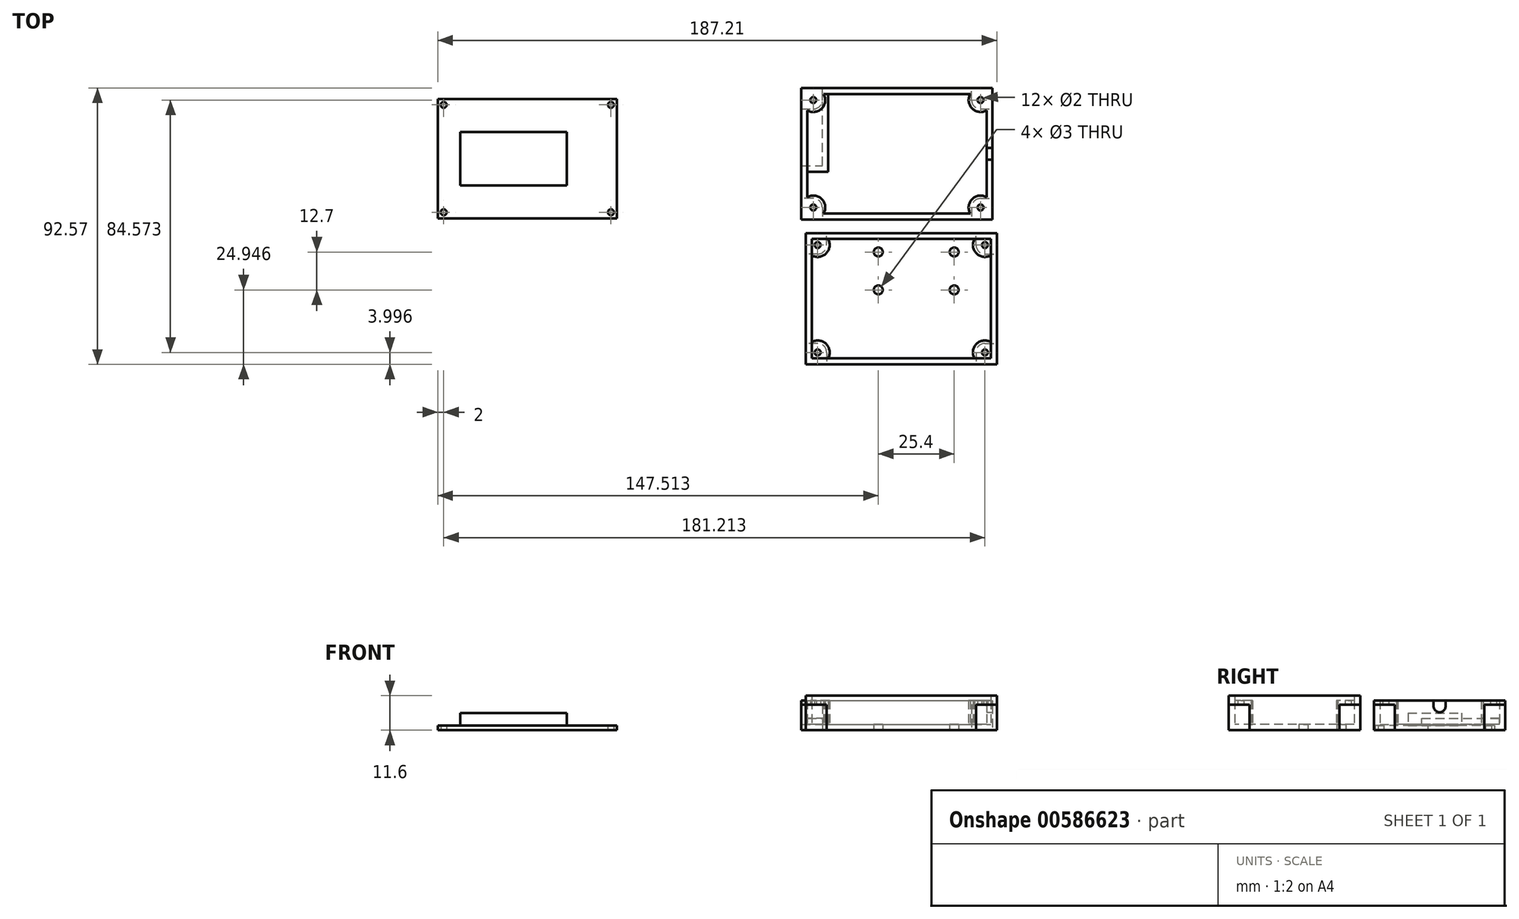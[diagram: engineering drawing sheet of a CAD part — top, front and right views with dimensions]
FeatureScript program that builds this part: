
annotation { "Feature Type Name" : "Feature", "Feature Type Description" : "" }
export const myFeature = defineFeature(function(context is Context, id is Id, definition is map)
    precondition{}
    {
        {
            var Q0;
            Q0=qCreatedBy(makeId("Top.planeOp"),FACE);
            var sketch = newSketch(context, id + "F0", { "sketchPlane" : qUnion([Q0])});
            skLineSegment(sketch, "E0.bottom", {"start": v(-101.7, 31.82) * mm, "end": v(-41.7, 31.82) * mm});
            skLineSegment(sketch, "E0.top", {"start": v(-101.7, -8.18) * mm, "end": v(-41.7, -8.18) * mm});
            skLineSegment(sketch, "E0.left", {"start": v(-101.7, 31.82) * mm, "end": v(-101.7, -8.18) * mm});
            skLineSegment(sketch, "E0.right", {"start": v(-41.7, 31.82) * mm, "end": v(-41.7, -8.18) * mm});
            skCircle(sketch, "E1", {"center": v(-99.7, 29.82) * mm, "radius": 1 * mm});
            skCircle(sketch, "E2", {"center": v(-99.7, -6.18) * mm, "radius": 1 * mm});
            skCircle(sketch, "E3", {"center": v(-43.7, 29.82) * mm, "radius": 1 * mm});
            skCircle(sketch, "E4", {"center": v(-43.7, -6.18) * mm, "radius": 1 * mm});
            skSolve(sketch);
        }
        {
            var Q0;
            Q0=qSketchRegion(id+"F0",true);
            extrude(context, id + "F1", {"entities" : qUnion([Q0]), "depth" : 1.6 * mm, "offsetDistance" : 25.4 * mm});
        }
        {
            var Q0;
            Q0=makeQuery(id+"F1.opExtrude","CAP_FACE",FACE,{"disambiguationData":[OSD([sQuery(id+"F0.wireOp",EDGE,"E0.bottom"),sQuery(id+"F0.wireOp",EDGE,"E0.top"),sQuery(id+"F0.wireOp",EDGE,"E0.left"),sQuery(id+"F0.wireOp",EDGE,"E0.right"),sQuery(id+"F0.wireOp",EDGE,"E1"),sQuery(id+"F0.wireOp",EDGE,"E2"),sQuery(id+"F0.wireOp",EDGE,"E3"),sQuery(id+"F0.wireOp",EDGE,"E4")])],"isStart":false});
            var sketch = newSketch(context, id + "F2", { "sketchPlane" : qUnion([Q0])});
            skSolve(sketch);
        }
        {
            var Q0;
            Q0=makeQuery(id+"F2.imprint","IMPRINT",FACE,{"disambiguationData":[TD([[makeQuery(id+"F2.imprint","IMPRINT",EDGE,{"derivedFrom":makeQuery(id+"F1.opExtrude","CAP_EDGE",EDGE,{"disambiguationData":[OSD([sQuery(id+"F0.wireOp",EDGE,"E0.bottom")])],"isStart":false})}),-1.0]])]});
            var sketch = newSketch(context, id + "F3", { "sketchPlane" : qUnion([Q0])});
            skLineSegment(sketch, "E5.bottom", {"start": v(-58.5, 2.87) * mm, "end": v(-94.2, 2.87) * mm});
            skLineSegment(sketch, "E5.top", {"start": v(-58.5, 20.77) * mm, "end": v(-94.2, 20.77) * mm});
            skLineSegment(sketch, "E5.left", {"start": v(-58.5, 2.87) * mm, "end": v(-58.5, 20.77) * mm});
            skLineSegment(sketch, "E5.right", {"start": v(-94.2, 2.87) * mm, "end": v(-94.2, 20.77) * mm});
            skPoint(sketch, "E6", {"position": v(-58.5, 11.82) * mm});
            skSolve(sketch);
        }
        {
            var Q0;
            Q0=makeQuery(id+"F3.imprint","IMPRINT",FACE,{"disambiguationData":[TD([[makeQuery(id+"F3.imprint","IMPRINT",EDGE,{"derivedFrom":sQuery(id+"F3.wireOp",EDGE,"E5.bottom")}),-1.0]])]});
            extrude(context, id + "F4", {"entities" : qUnion([Q0]), "operationType" : NewBodyOperationType.ADD, "depth" : 4.2 * mm, "offsetDistance" : 25.4 * mm});
        }
        {
            var Q0;
            Q0=qCreatedBy(makeId("Top.planeOp"),FACE);
            var sketch = newSketch(context, id + "F5", { "sketchPlane" : qUnion([Q0])});
            skLineSegment(sketch, "E7.bottom", {"start": v(20.05, 35.44) * mm, "end": v(84.05, 35.44) * mm});
            skLineSegment(sketch, "E7.top", {"start": v(20.05, -8.56) * mm, "end": v(84.05, -8.56) * mm});
            skLineSegment(sketch, "E7.left", {"start": v(20.05, 35.44) * mm, "end": v(20.05, -8.56) * mm});
            skLineSegment(sketch, "E7.right", {"start": v(84.05, 35.44) * mm, "end": v(84.05, -8.56) * mm});
            skCircle(sketch, "E8", {"center": v(24.05, 31.44) * mm, "radius": 1 * mm});
            skCircle(sketch, "E9", {"center": v(24.05, -4.56) * mm, "radius": 1 * mm});
            skCircle(sketch, "E10", {"center": v(80.05, 31.44) * mm, "radius": 1 * mm});
            skCircle(sketch, "E11", {"center": v(80.05, -4.56) * mm, "radius": 1 * mm});
            skSolve(sketch);
        }
        {
            var Q0;
            Q0=makeQuery(id+"F5.imprint","IMPRINT",FACE,{"disambiguationData":[TD([[makeQuery(id+"F5.imprint","IMPRINT",EDGE,{"derivedFrom":sQuery(id+"F5.wireOp",EDGE,"E7.bottom")}),-1.0]])]});
            extrude(context, id + "F6", {"entities" : qUnion([Q0]), "depth" : 2 * mm, "offsetDistance" : 25.4 * mm});
        }
        {
            var Q0;
            Q0=makeQuery(id+"F6.opExtrude","CAP_FACE",FACE,{"disambiguationData":[OSD([sQuery(id+"F5.wireOp",EDGE,"E7.bottom"),sQuery(id+"F5.wireOp",EDGE,"E7.top"),sQuery(id+"F5.wireOp",EDGE,"E7.left"),sQuery(id+"F5.wireOp",EDGE,"E7.right"),sQuery(id+"F5.wireOp",EDGE,"E8"),sQuery(id+"F5.wireOp",EDGE,"E9"),sQuery(id+"F5.wireOp",EDGE,"E10"),sQuery(id+"F5.wireOp",EDGE,"E11")])],"isStart":false});
            var sketch = newSketch(context, id + "F7", { "sketchPlane" : qUnion([Q0])});
            skCircle(sketch, "E12", {"center": v(24.05, 31.44) * mm, "radius": 4 * mm});
            skCircle(sketch, "E13", {"center": v(24.05, -4.56) * mm, "radius": 4 * mm});
            skCircle(sketch, "E14", {"center": v(80.05, 31.44) * mm, "radius": 4 * mm});
            skCircle(sketch, "E15", {"center": v(80.05, -4.56) * mm, "radius": 4 * mm});
            skLineSegment(sketch, "E16.bottom", {"start": v(20.05, 35.44) * mm, "end": v(84.05, 35.44) * mm});
            skLineSegment(sketch, "E16.top", {"start": v(20.05, -8.56) * mm, "end": v(84.05, -8.56) * mm});
            skLineSegment(sketch, "E16.left", {"start": v(20.05, 35.44) * mm, "end": v(20.05, -8.56) * mm});
            skLineSegment(sketch, "E16.right", {"start": v(84.05, 35.44) * mm, "end": v(84.05, -8.56) * mm});
            skLineSegment(sketch, "E17.bottom", {"start": v(22.05, 33.44) * mm, "end": v(82.05, 33.44) * mm});
            skLineSegment(sketch, "E17.top", {"start": v(22.05, -6.56) * mm, "end": v(82.05, -6.56) * mm});
            skLineSegment(sketch, "E17.left", {"start": v(22.05, 33.44) * mm, "end": v(22.05, -6.56) * mm});
            skLineSegment(sketch, "E17.right", {"start": v(82.05, 33.44) * mm, "end": v(82.05, -6.56) * mm});
            skSolve(sketch);
        }
        {
            var Q0;
            Q0=qSketchRegion(id+"F7",true);
            var Q1;
            Q1=makeQuery(id+"F7.imprint","IMPRINT",FACE,{"disambiguationData":[TD([[makeQuery(id+"F7.imprint","IMPRINT",EDGE,{"derivedFrom":makeQuery(id+"F6.opExtrude","CAP_EDGE",EDGE,{"disambiguationData":[OSD([sQuery(id+"F5.wireOp",EDGE,"E8")])],"isStart":false})}),-1.0]])]});
            var Q2;
            {var subQ0=sQuery(id+"F7.wireOp",EDGE,"E17.left");var subQ1=sQuery(id+"F7.wireOp",EDGE,"E12");var subQ2=makeQuery(id+"F7.imprint","INTERSECT",VERTEX,{"disambiguationData":[OD(0.0)],"derivedFrom":[subQ1,subQ0]});Q2=makeQuery(id+"F7.imprint","IMPRINT",FACE,{"disambiguationData":[TD([[makeQuery(id+"F7.imprint","IMPRINT",EDGE,{"disambiguationData":[TD([[subQ2,-1.0]])],"derivedFrom":subQ1}),1.0]])]});}
            var Q3;
            {var subQ0=sQuery(id+"F7.wireOp",EDGE,"E17.bottom");var subQ1=sQuery(id+"F7.wireOp",EDGE,"E12");var subQ2=makeQuery(id+"F7.imprint","INTERSECT",VERTEX,{"disambiguationData":[OD(0.0)],"derivedFrom":[subQ1,subQ0]});Q3=makeQuery(id+"F7.imprint","IMPRINT",FACE,{"disambiguationData":[TD([[makeQuery(id+"F7.imprint","IMPRINT",EDGE,{"disambiguationData":[TD([[subQ2,1.0]])],"derivedFrom":subQ1}),1.0]])]});}
            var Q4;
            {var subQ0=sQuery(id+"F7.wireOp",EDGE,"E17.bottom");var subQ1=sQuery(id+"F7.wireOp",EDGE,"E12");var subQ2=makeQuery(id+"F7.imprint","INTERSECT",VERTEX,{"disambiguationData":[OD(0.0)],"derivedFrom":[subQ1,subQ0]});Q4=makeQuery(id+"F7.imprint","IMPRINT",FACE,{"disambiguationData":[TD([[makeQuery(id+"F7.imprint","IMPRINT",EDGE,{"disambiguationData":[TD([[subQ2,-1.0]])],"derivedFrom":subQ1}),-1.0]])]});}
            var Q5;
            {var subQ0=sQuery(id+"F7.wireOp",EDGE,"E17.left");var subQ1=sQuery(id+"F7.wireOp",EDGE,"E13");var subQ2=makeQuery(id+"F7.imprint","INTERSECT",VERTEX,{"disambiguationData":[OD(0.0)],"derivedFrom":[subQ1,subQ0]});Q5=makeQuery(id+"F7.imprint","IMPRINT",FACE,{"disambiguationData":[TD([[makeQuery(id+"F7.imprint","IMPRINT",EDGE,{"disambiguationData":[TD([[subQ2,-1.0]])],"derivedFrom":subQ1}),-1.0]])]});}
            var Q6;
            {var subQ0=sQuery(id+"F7.wireOp",EDGE,"E17.top");var subQ1=sQuery(id+"F7.wireOp",EDGE,"E13");var subQ2=makeQuery(id+"F7.imprint","INTERSECT",VERTEX,{"disambiguationData":[OD(0.0)],"derivedFrom":[subQ1,subQ0]});Q6=makeQuery(id+"F7.imprint","IMPRINT",FACE,{"disambiguationData":[TD([[makeQuery(id+"F7.imprint","IMPRINT",EDGE,{"disambiguationData":[TD([[subQ2,-1.0]])],"derivedFrom":subQ1}),1.0]])]});}
            var Q7;
            {var subQ0=sQuery(id+"F7.wireOp",EDGE,"E17.left");var subQ1=sQuery(id+"F7.wireOp",EDGE,"E13");var subQ2=makeQuery(id+"F7.imprint","INTERSECT",VERTEX,{"disambiguationData":[OD(0.0)],"derivedFrom":[subQ1,subQ0]});Q7=makeQuery(id+"F7.imprint","IMPRINT",FACE,{"disambiguationData":[TD([[makeQuery(id+"F7.imprint","IMPRINT",EDGE,{"disambiguationData":[TD([[subQ2,1.0]])],"derivedFrom":subQ1}),1.0]])]});}
            var Q8;
            Q8=makeQuery(id+"F7.imprint","IMPRINT",FACE,{"disambiguationData":[TD([[makeQuery(id+"F7.imprint","IMPRINT",EDGE,{"derivedFrom":makeQuery(id+"F6.opExtrude","CAP_EDGE",EDGE,{"disambiguationData":[OSD([sQuery(id+"F5.wireOp",EDGE,"E9")])],"isStart":false})}),-1.0]])]});
            var Q9;
            {var subQ0=sQuery(id+"F7.wireOp",EDGE,"E17.top");var subQ1=sQuery(id+"F7.wireOp",EDGE,"E15");var subQ2=makeQuery(id+"F7.imprint","INTERSECT",VERTEX,{"disambiguationData":[OD(1.0)],"derivedFrom":[subQ1,subQ0]});Q9=makeQuery(id+"F7.imprint","IMPRINT",FACE,{"disambiguationData":[TD([[makeQuery(id+"F7.imprint","IMPRINT",EDGE,{"disambiguationData":[TD([[subQ2,-1.0]])],"derivedFrom":subQ1}),-1.0]])]});}
            var Q10;
            {var subQ0=sQuery(id+"F7.wireOp",EDGE,"E17.right");var subQ1=sQuery(id+"F7.wireOp",EDGE,"E15");var subQ2=makeQuery(id+"F7.imprint","INTERSECT",VERTEX,{"disambiguationData":[OD(0.0)],"derivedFrom":[subQ1,subQ0]});Q10=makeQuery(id+"F7.imprint","IMPRINT",FACE,{"disambiguationData":[TD([[makeQuery(id+"F7.imprint","IMPRINT",EDGE,{"disambiguationData":[TD([[subQ2,1.0]])],"derivedFrom":subQ1}),1.0]])]});}
            var Q11;
            {var subQ0=sQuery(id+"F7.wireOp",EDGE,"E17.top");var subQ1=sQuery(id+"F7.wireOp",EDGE,"E15");var subQ2=makeQuery(id+"F7.imprint","INTERSECT",VERTEX,{"disambiguationData":[OD(0.0)],"derivedFrom":[subQ1,subQ0]});Q11=makeQuery(id+"F7.imprint","IMPRINT",FACE,{"disambiguationData":[TD([[makeQuery(id+"F7.imprint","IMPRINT",EDGE,{"disambiguationData":[TD([[subQ2,-1.0]])],"derivedFrom":subQ1}),1.0]])]});}
            var Q12;
            Q12=makeQuery(id+"F7.imprint","IMPRINT",FACE,{"disambiguationData":[TD([[makeQuery(id+"F7.imprint","IMPRINT",EDGE,{"derivedFrom":makeQuery(id+"F6.opExtrude","CAP_EDGE",EDGE,{"disambiguationData":[OSD([sQuery(id+"F5.wireOp",EDGE,"E11")])],"isStart":false})}),-1.0]])]});
            var Q13;
            {var subQ0=sQuery(id+"F7.wireOp",EDGE,"E17.right");var subQ1=sQuery(id+"F7.wireOp",EDGE,"E14");var subQ2=makeQuery(id+"F7.imprint","INTERSECT",VERTEX,{"disambiguationData":[OD(0.0)],"derivedFrom":[subQ1,subQ0]});Q13=makeQuery(id+"F7.imprint","IMPRINT",FACE,{"disambiguationData":[TD([[makeQuery(id+"F7.imprint","IMPRINT",EDGE,{"disambiguationData":[TD([[subQ2,1.0]])],"derivedFrom":subQ1}),1.0]])]});}
            var Q14;
            {var subQ0=sQuery(id+"F7.wireOp",EDGE,"E17.bottom");var subQ1=sQuery(id+"F7.wireOp",EDGE,"E14");var subQ2=makeQuery(id+"F7.imprint","INTERSECT",VERTEX,{"disambiguationData":[OD(0.0)],"derivedFrom":[subQ1,subQ0]});Q14=makeQuery(id+"F7.imprint","IMPRINT",FACE,{"disambiguationData":[TD([[makeQuery(id+"F7.imprint","IMPRINT",EDGE,{"disambiguationData":[TD([[subQ2,1.0]])],"derivedFrom":subQ1}),-1.0]])]});}
            var Q15;
            {var subQ0=sQuery(id+"F7.wireOp",EDGE,"E17.bottom");var subQ1=sQuery(id+"F7.wireOp",EDGE,"E14");var subQ2=makeQuery(id+"F7.imprint","INTERSECT",VERTEX,{"disambiguationData":[OD(0.0)],"derivedFrom":[subQ1,subQ0]});Q15=makeQuery(id+"F7.imprint","IMPRINT",FACE,{"disambiguationData":[TD([[makeQuery(id+"F7.imprint","IMPRINT",EDGE,{"disambiguationData":[TD([[subQ2,-1.0]])],"derivedFrom":subQ1}),1.0]])]});}
            var Q16;
            Q16=makeQuery(id+"F7.imprint","IMPRINT",FACE,{"disambiguationData":[TD([[makeQuery(id+"F7.imprint","IMPRINT",EDGE,{"derivedFrom":makeQuery(id+"F6.opExtrude","CAP_EDGE",EDGE,{"disambiguationData":[OSD([sQuery(id+"F5.wireOp",EDGE,"E10")])],"isStart":false})}),-1.0]])]});
            var Q17;
            {var subQ0=sQuery(id+"F7.wireOp",EDGE,"E17.bottom");var subQ1=sQuery(id+"F7.wireOp",EDGE,"E14");var subQ2=makeQuery(id+"F7.imprint","INTERSECT",VERTEX,{"derivedFrom":[subQ1,subQ0]});Q17=makeQuery(id+"F7.imprint","IMPRINT",FACE,{"disambiguationData":[TD([[makeQuery(id+"F7.imprint","IMPRINT",EDGE,{"disambiguationData":[TD([[subQ2,1.0]])],"derivedFrom":subQ1}),1.0]])]});}
            extrude(context, id + "F8", {"entities" : qUnion([Q0, Q1, Q2, Q3, Q4, Q5, Q6, Q7, Q8, Q9, Q10, Q11, Q12, Q13, Q14, Q15, Q16, Q17]), "operationType" : NewBodyOperationType.ADD, "depth" : 8 * mm, "offsetDistance" : 25.4 * mm});
        }
        {
            var Q0;
            Q0=qCreatedBy(makeId("Top.planeOp"),FACE);
            var sketch = newSketch(context, id + "F9", { "sketchPlane" : qUnion([Q0])});
            skLineSegment(sketch, "E18.bottom", {"start": v(21.5, -13.13) * mm, "end": v(85.5, -13.13) * mm});
            skLineSegment(sketch, "E18.top", {"start": v(21.5, -57.13) * mm, "end": v(85.5, -57.13) * mm});
            skLineSegment(sketch, "E18.left", {"start": v(21.5, -13.13) * mm, "end": v(21.5, -57.13) * mm});
            skLineSegment(sketch, "E18.right", {"start": v(85.5, -13.13) * mm, "end": v(85.5, -57.13) * mm});
            skCircle(sketch, "E19", {"center": v(25.5, -17.13) * mm, "radius": 1 * mm});
            skCircle(sketch, "E20", {"center": v(25.5, -53.13) * mm, "radius": 1 * mm});
            skCircle(sketch, "E21", {"center": v(81.5, -17.13) * mm, "radius": 1 * mm});
            skCircle(sketch, "E22", {"center": v(81.5, -53.13) * mm, "radius": 1 * mm});
            skSolve(sketch);
        }
        {
            var Q0;
            Q0=qSketchRegion(id+"F9",true);
            extrude(context, id + "F10", {"entities" : qUnion([Q0]), "depth" : 2 * mm, "offsetDistance" : 25.4 * mm});
        }
        {
            var Q0;
            Q0=makeQuery(id+"F10.opExtrude","CAP_FACE",FACE,{"disambiguationData":[OSD([sQuery(id+"F9.wireOp",EDGE,"E18.bottom"),sQuery(id+"F9.wireOp",EDGE,"E18.top"),sQuery(id+"F9.wireOp",EDGE,"E18.left"),sQuery(id+"F9.wireOp",EDGE,"E18.right"),sQuery(id+"F9.wireOp",EDGE,"E19"),sQuery(id+"F9.wireOp",EDGE,"E20"),sQuery(id+"F9.wireOp",EDGE,"E21"),sQuery(id+"F9.wireOp",EDGE,"E22")])],"isStart":false});
            var sketch = newSketch(context, id + "F11", { "sketchPlane" : qUnion([Q0])});
            skCircle(sketch, "E23", {"center": v(25.5, -17.13) * mm, "radius": 4 * mm});
            skCircle(sketch, "E24", {"center": v(81.5, -17.13) * mm, "radius": 4 * mm});
            skCircle(sketch, "E25", {"center": v(25.5, -53.13) * mm, "radius": 4 * mm});
            skCircle(sketch, "E26", {"center": v(81.5, -53.13) * mm, "radius": 4 * mm});
            skLineSegment(sketch, "E27.bottom", {"start": v(21.5, -13.13) * mm, "end": v(85.5, -13.13) * mm});
            skLineSegment(sketch, "E27.top", {"start": v(21.5, -57.13) * mm, "end": v(85.5, -57.13) * mm});
            skLineSegment(sketch, "E27.left", {"start": v(21.5, -13.13) * mm, "end": v(21.5, -57.13) * mm});
            skLineSegment(sketch, "E27.right", {"start": v(85.5, -13.13) * mm, "end": v(85.5, -57.13) * mm});
            skLineSegment(sketch, "E28.bottom", {"start": v(23.5, -15.13) * mm, "end": v(83.5, -15.13) * mm});
            skLineSegment(sketch, "E28.top", {"start": v(23.5, -55.13) * mm, "end": v(83.5, -55.13) * mm});
            skLineSegment(sketch, "E28.left", {"start": v(23.5, -15.13) * mm, "end": v(23.5, -55.13) * mm});
            skLineSegment(sketch, "E28.right", {"start": v(83.5, -15.13) * mm, "end": v(83.5, -55.13) * mm});
            skSolve(sketch);
        }
        {
            var Q0;
            Q0=qSketchRegion(id+"F11",true);
            var Q1;
            {var subQ0=sQuery(id+"F11.wireOp",EDGE,"E28.left");var subQ1=sQuery(id+"F11.wireOp",EDGE,"E25");var subQ2=makeQuery(id+"F11.imprint","INTERSECT",VERTEX,{"disambiguationData":[OD(0.0)],"derivedFrom":[subQ1,subQ0]});Q1=makeQuery(id+"F11.imprint","IMPRINT",FACE,{"disambiguationData":[TD([[makeQuery(id+"F11.imprint","IMPRINT",EDGE,{"disambiguationData":[TD([[subQ2,-1.0]])],"derivedFrom":subQ1}),-1.0]])]});}
            var Q2;
            {var subQ0=sQuery(id+"F11.wireOp",EDGE,"E28.left");var subQ1=sQuery(id+"F11.wireOp",EDGE,"E25");var subQ2=makeQuery(id+"F11.imprint","INTERSECT",VERTEX,{"disambiguationData":[OD(0.0)],"derivedFrom":[subQ1,subQ0]});Q2=makeQuery(id+"F11.imprint","IMPRINT",FACE,{"disambiguationData":[TD([[makeQuery(id+"F11.imprint","IMPRINT",EDGE,{"disambiguationData":[TD([[subQ2,1.0]])],"derivedFrom":subQ1}),1.0]])]});}
            var Q3;
            {var subQ0=sQuery(id+"F11.wireOp",EDGE,"E28.top");var subQ1=sQuery(id+"F11.wireOp",EDGE,"E25");var subQ2=makeQuery(id+"F11.imprint","INTERSECT",VERTEX,{"disambiguationData":[OD(0.0)],"derivedFrom":[subQ1,subQ0]});Q3=makeQuery(id+"F11.imprint","IMPRINT",FACE,{"disambiguationData":[TD([[makeQuery(id+"F11.imprint","IMPRINT",EDGE,{"disambiguationData":[TD([[subQ2,-1.0]])],"derivedFrom":subQ1}),1.0]])]});}
            var Q4;
            Q4=makeQuery(id+"F11.imprint","IMPRINT",FACE,{"disambiguationData":[TD([[makeQuery(id+"F11.imprint","IMPRINT",EDGE,{"derivedFrom":makeQuery(id+"F10.opExtrude","CAP_EDGE",EDGE,{"disambiguationData":[OSD([sQuery(id+"F9.wireOp",EDGE,"E20")])],"isStart":false})}),-1.0]])]});
            var Q5;
            {var subQ0=sQuery(id+"F11.wireOp",EDGE,"E28.bottom");var subQ1=sQuery(id+"F11.wireOp",EDGE,"E23");var subQ2=makeQuery(id+"F11.imprint","INTERSECT",VERTEX,{"disambiguationData":[OD(0.0)],"derivedFrom":[subQ1,subQ0]});Q5=makeQuery(id+"F11.imprint","IMPRINT",FACE,{"disambiguationData":[TD([[makeQuery(id+"F11.imprint","IMPRINT",EDGE,{"disambiguationData":[TD([[subQ2,-1.0]])],"derivedFrom":subQ1}),-1.0]])]});}
            var Q6;
            {var subQ0=sQuery(id+"F11.wireOp",EDGE,"E28.left");var subQ1=sQuery(id+"F11.wireOp",EDGE,"E23");var subQ2=makeQuery(id+"F11.imprint","INTERSECT",VERTEX,{"disambiguationData":[OD(0.0)],"derivedFrom":[subQ1,subQ0]});Q6=makeQuery(id+"F11.imprint","IMPRINT",FACE,{"disambiguationData":[TD([[makeQuery(id+"F11.imprint","IMPRINT",EDGE,{"disambiguationData":[TD([[subQ2,-1.0]])],"derivedFrom":subQ1}),1.0]])]});}
            var Q7;
            {var subQ0=sQuery(id+"F11.wireOp",EDGE,"E28.bottom");var subQ1=sQuery(id+"F11.wireOp",EDGE,"E23");var subQ2=makeQuery(id+"F11.imprint","INTERSECT",VERTEX,{"disambiguationData":[OD(0.0)],"derivedFrom":[subQ1,subQ0]});Q7=makeQuery(id+"F11.imprint","IMPRINT",FACE,{"disambiguationData":[TD([[makeQuery(id+"F11.imprint","IMPRINT",EDGE,{"disambiguationData":[TD([[subQ2,1.0]])],"derivedFrom":subQ1}),1.0]])]});}
            var Q8;
            Q8=makeQuery(id+"F11.imprint","IMPRINT",FACE,{"disambiguationData":[TD([[makeQuery(id+"F11.imprint","IMPRINT",EDGE,{"derivedFrom":makeQuery(id+"F10.opExtrude","CAP_EDGE",EDGE,{"disambiguationData":[OSD([sQuery(id+"F9.wireOp",EDGE,"E19")])],"isStart":false})}),-1.0]])]});
            var Q9;
            {var subQ0=sQuery(id+"F11.wireOp",EDGE,"E28.bottom");var subQ1=sQuery(id+"F11.wireOp",EDGE,"E24");var subQ2=makeQuery(id+"F11.imprint","INTERSECT",VERTEX,{"disambiguationData":[OD(0.0)],"derivedFrom":[subQ1,subQ0]});Q9=makeQuery(id+"F11.imprint","IMPRINT",FACE,{"disambiguationData":[TD([[makeQuery(id+"F11.imprint","IMPRINT",EDGE,{"disambiguationData":[TD([[subQ2,1.0]])],"derivedFrom":subQ1}),-1.0]])]});}
            var Q10;
            {var subQ0=sQuery(id+"F11.wireOp",EDGE,"E28.right");var subQ1=sQuery(id+"F11.wireOp",EDGE,"E24");var subQ2=makeQuery(id+"F11.imprint","INTERSECT",VERTEX,{"disambiguationData":[OD(0.0)],"derivedFrom":[subQ1,subQ0]});Q10=makeQuery(id+"F11.imprint","IMPRINT",FACE,{"disambiguationData":[TD([[makeQuery(id+"F11.imprint","IMPRINT",EDGE,{"disambiguationData":[TD([[subQ2,1.0]])],"derivedFrom":subQ1}),1.0]])]});}
            var Q11;
            {var subQ0=sQuery(id+"F11.wireOp",EDGE,"E28.bottom");var subQ1=sQuery(id+"F11.wireOp",EDGE,"E24");var subQ2=makeQuery(id+"F11.imprint","INTERSECT",VERTEX,{"disambiguationData":[OD(0.0)],"derivedFrom":[subQ1,subQ0]});Q11=makeQuery(id+"F11.imprint","IMPRINT",FACE,{"disambiguationData":[TD([[makeQuery(id+"F11.imprint","IMPRINT",EDGE,{"disambiguationData":[TD([[subQ2,-1.0]])],"derivedFrom":subQ1}),1.0]])]});}
            var Q12;
            Q12=makeQuery(id+"F11.imprint","IMPRINT",FACE,{"disambiguationData":[TD([[makeQuery(id+"F11.imprint","IMPRINT",EDGE,{"derivedFrom":makeQuery(id+"F10.opExtrude","CAP_EDGE",EDGE,{"disambiguationData":[OSD([sQuery(id+"F9.wireOp",EDGE,"E21")])],"isStart":false})}),-1.0]])]});
            var Q13;
            {var subQ0=sQuery(id+"F11.wireOp",EDGE,"E28.top");var subQ1=sQuery(id+"F11.wireOp",EDGE,"E26");var subQ2=makeQuery(id+"F11.imprint","INTERSECT",VERTEX,{"disambiguationData":[OD(1.0)],"derivedFrom":[subQ1,subQ0]});Q13=makeQuery(id+"F11.imprint","IMPRINT",FACE,{"disambiguationData":[TD([[makeQuery(id+"F11.imprint","IMPRINT",EDGE,{"disambiguationData":[TD([[subQ2,-1.0]])],"derivedFrom":subQ1}),-1.0]])]});}
            var Q14;
            {var subQ0=sQuery(id+"F11.wireOp",EDGE,"E28.right");var subQ1=sQuery(id+"F11.wireOp",EDGE,"E26");var subQ2=makeQuery(id+"F11.imprint","INTERSECT",VERTEX,{"disambiguationData":[OD(0.0)],"derivedFrom":[subQ1,subQ0]});Q14=makeQuery(id+"F11.imprint","IMPRINT",FACE,{"disambiguationData":[TD([[makeQuery(id+"F11.imprint","IMPRINT",EDGE,{"disambiguationData":[TD([[subQ2,1.0]])],"derivedFrom":subQ1}),1.0]])]});}
            var Q15;
            {var subQ0=sQuery(id+"F11.wireOp",EDGE,"E28.top");var subQ1=sQuery(id+"F11.wireOp",EDGE,"E26");var subQ2=makeQuery(id+"F11.imprint","INTERSECT",VERTEX,{"disambiguationData":[OD(0.0)],"derivedFrom":[subQ1,subQ0]});Q15=makeQuery(id+"F11.imprint","IMPRINT",FACE,{"disambiguationData":[TD([[makeQuery(id+"F11.imprint","IMPRINT",EDGE,{"disambiguationData":[TD([[subQ2,-1.0]])],"derivedFrom":subQ1}),1.0]])]});}
            var Q16;
            Q16=makeQuery(id+"F11.imprint","IMPRINT",FACE,{"disambiguationData":[TD([[makeQuery(id+"F11.imprint","IMPRINT",EDGE,{"derivedFrom":makeQuery(id+"F10.opExtrude","CAP_EDGE",EDGE,{"disambiguationData":[OSD([sQuery(id+"F9.wireOp",EDGE,"E22")])],"isStart":false})}),-1.0]])]});
            var Q17;
            {var subQ0=sQuery(id+"F11.wireOp",EDGE,"E28.top");var subQ1=sQuery(id+"F11.wireOp",EDGE,"E25");var subQ2=makeQuery(id+"F11.imprint","INTERSECT",VERTEX,{"derivedFrom":[subQ1,subQ0]});Q17=makeQuery(id+"F11.imprint","IMPRINT",FACE,{"disambiguationData":[TD([[makeQuery(id+"F11.imprint","IMPRINT",EDGE,{"disambiguationData":[TD([[subQ2,1.0]])],"derivedFrom":subQ1}),1.0]])]});}
            var Q18;
            {var subQ0=sQuery(id+"F11.wireOp",EDGE,"E28.bottom");var subQ1=sQuery(id+"F11.wireOp",EDGE,"E23");var subQ2=makeQuery(id+"F11.imprint","INTERSECT",VERTEX,{"derivedFrom":[subQ1,subQ0]});Q18=makeQuery(id+"F11.imprint","IMPRINT",FACE,{"disambiguationData":[TD([[makeQuery(id+"F11.imprint","IMPRINT",EDGE,{"disambiguationData":[TD([[subQ2,-1.0]])],"derivedFrom":subQ1}),1.0]])]});}
            var Q19;
            {var subQ0=sQuery(id+"F11.wireOp",EDGE,"E28.bottom");var subQ1=sQuery(id+"F11.wireOp",EDGE,"E24");var subQ2=makeQuery(id+"F11.imprint","INTERSECT",VERTEX,{"derivedFrom":[subQ1,subQ0]});Q19=makeQuery(id+"F11.imprint","IMPRINT",FACE,{"disambiguationData":[TD([[makeQuery(id+"F11.imprint","IMPRINT",EDGE,{"disambiguationData":[TD([[subQ2,1.0]])],"derivedFrom":subQ1}),1.0]])]});}
            extrude(context, id + "F12", {"entities" : qUnion([Q0, Q1, Q2, Q3, Q4, Q5, Q6, Q7, Q8, Q9, Q10, Q11, Q12, Q13, Q14, Q15, Q16, Q17, Q18, Q19]), "operationType" : NewBodyOperationType.ADD, "depth" : 8 * mm, "offsetDistance" : 25.4 * mm});
        }
        {
            var Q0;
            Q0=makeQuery(id+"F12.opExtrude","CAP_FACE",FACE,{"disambiguationData":[OSD([sQuery(id+"F9.wireOp",EDGE,"E19"),sQuery(id+"F9.wireOp",EDGE,"E20"),sQuery(id+"F9.wireOp",EDGE,"E21"),sQuery(id+"F9.wireOp",EDGE,"E22"),sQuery(id+"F11.wireOp",EDGE,"E23"),sQuery(id+"F11.wireOp",EDGE,"E24"),sQuery(id+"F11.wireOp",EDGE,"E25"),sQuery(id+"F11.wireOp",EDGE,"E26"),sQuery(id+"F11.wireOp",EDGE,"E27.bottom"),sQuery(id+"F11.wireOp",EDGE,"E27.top"),sQuery(id+"F11.wireOp",EDGE,"E27.left"),sQuery(id+"F11.wireOp",EDGE,"E27.right"),sQuery(id+"F11.wireOp",EDGE,"E28.bottom"),sQuery(id+"F11.wireOp",EDGE,"E28.top"),sQuery(id+"F11.wireOp",EDGE,"E28.left"),sQuery(id+"F11.wireOp",EDGE,"E28.right")])],"isStart":false});
            var sketch = newSketch(context, id + "F13", { "sketchPlane" : qUnion([Q0])});
            skLineSegment(sketch, "E29.bottom", {"start": v(21.5, -13.13) * mm, "end": v(85.5, -13.13) * mm});
            skLineSegment(sketch, "E29.top", {"start": v(21.5, -57.13) * mm, "end": v(85.5, -57.13) * mm});
            skLineSegment(sketch, "E29.left", {"start": v(21.5, -13.13) * mm, "end": v(21.5, -57.13) * mm});
            skLineSegment(sketch, "E29.right", {"start": v(85.5, -13.13) * mm, "end": v(85.5, -57.13) * mm});
            skLineSegment(sketch, "E30.bottom", {"start": v(23.5, -15.13) * mm, "end": v(83.5, -15.13) * mm});
            skLineSegment(sketch, "E30.top", {"start": v(23.5, -55.13) * mm, "end": v(83.5, -55.13) * mm});
            skLineSegment(sketch, "E30.left", {"start": v(23.5, -15.13) * mm, "end": v(23.5, -55.13) * mm});
            skLineSegment(sketch, "E30.right", {"start": v(83.5, -15.13) * mm, "end": v(83.5, -55.13) * mm});
            skSolve(sketch);
        }
        {
            var Q0;
            Q0=qSketchRegion(id+"F13",true);
            extrude(context, id + "F14", {"entities" : qUnion([Q0]), "operationType" : NewBodyOperationType.ADD, "depth" : 1.6 * mm, "offsetDistance" : 25.4 * mm});
        }
        {
            var Q0;
            Q0=makeQuery(id+"F10.opExtrude","CAP_FACE",FACE,{"disambiguationData":[OSD([sQuery(id+"F9.wireOp",EDGE,"E18.bottom"),sQuery(id+"F9.wireOp",EDGE,"E18.top"),sQuery(id+"F9.wireOp",EDGE,"E18.left"),sQuery(id+"F9.wireOp",EDGE,"E18.right"),sQuery(id+"F9.wireOp",EDGE,"E19"),sQuery(id+"F9.wireOp",EDGE,"E20"),sQuery(id+"F9.wireOp",EDGE,"E21"),sQuery(id+"F9.wireOp",EDGE,"E22")])],"isStart":true});
            var sketch = newSketch(context, id + "F15", { "sketchPlane" : qUnion([Q0])});
            skCircle(sketch, "E31", {"center": v(81.5, 53.13) * mm, "radius": 3 * mm});
            skLineSegment(sketch, "E32", {"start": v(81.5, 50.13) * mm, "end": v(85.5, 50.13) * mm});
            skLineSegment(sketch, "E33", {"start": v(78.5, 53.13) * mm, "end": v(78.5, 57.13) * mm});
            skCircle(sketch, "E34", {"center": v(81.5, 17.13) * mm, "radius": 3 * mm});
            skCircle(sketch, "E35", {"center": v(25.5, 53.13) * mm, "radius": 3 * mm});
            skCircle(sketch, "E36", {"center": v(25.5, 17.13) * mm, "radius": 3 * mm});
            skLineSegment(sketch, "E37", {"start": v(81.5, 20.13) * mm, "end": v(85.5, 20.13) * mm});
            skLineSegment(sketch, "E38", {"start": v(78.5, 17.13) * mm, "end": v(78.5, 13.13) * mm});
            skLineSegment(sketch, "E39", {"start": v(28.5, 53.13) * mm, "end": v(28.5, 57.13) * mm});
            skLineSegment(sketch, "E40", {"start": v(25.5, 50.13) * mm, "end": v(21.5, 50.13) * mm});
            skLineSegment(sketch, "E41", {"start": v(25.5, 20.13) * mm, "end": v(21.5, 20.13) * mm});
            skLineSegment(sketch, "E42", {"start": v(28.5, 17.13) * mm, "end": v(28.5, 13.13) * mm});
            skSolve(sketch);
        }
        {
            var Q0;
            Q0=qSketchRegion(id+"F15",true);
            var Q1;
            {var subQ3=sQuery(id+"F15.wireOp",EDGE,"E39");Q1=makeQuery(id+"F15.imprint","IMPRINT",FACE,{"disambiguationData":[TD([[makeQuery(id+"F15.imprint","IMPRINT",EDGE,{"derivedFrom":subQ3}),1.0]])]});}
            var Q2;
            {var subQ4=sQuery(id+"F15.wireOp",EDGE,"E41");Q2=makeQuery(id+"F15.imprint","IMPRINT",FACE,{"disambiguationData":[TD([[makeQuery(id+"F15.imprint","IMPRINT",EDGE,{"derivedFrom":subQ4}),1.0]])]});}
            var Q3;
            {var subQ4=sQuery(id+"F15.wireOp",EDGE,"E37");Q3=makeQuery(id+"F15.imprint","IMPRINT",FACE,{"disambiguationData":[TD([[makeQuery(id+"F15.imprint","IMPRINT",EDGE,{"derivedFrom":subQ4}),-1.0]])]});}
            var Q4;
            {var subQ4=sQuery(id+"F15.wireOp",EDGE,"E32");Q4=makeQuery(id+"F15.imprint","IMPRINT",FACE,{"disambiguationData":[TD([[makeQuery(id+"F15.imprint","IMPRINT",EDGE,{"derivedFrom":subQ4}),1.0]])]});}
            extrude(context, id + "F16", {"entities" : qUnion([Q0, Q1, Q2, Q3, Q4]), "operationType" : NewBodyOperationType.REMOVE, "oppositeDirection" : true, "depth" : 8.5 * mm, "offsetDistance" : 25.4 * mm});
        }
        {
            var Q0;
            Q0=makeQuery(id+"F6.opExtrude","CAP_FACE",FACE,{"disambiguationData":[OSD([sQuery(id+"F5.wireOp",EDGE,"E7.bottom"),sQuery(id+"F5.wireOp",EDGE,"E7.top"),sQuery(id+"F5.wireOp",EDGE,"E7.left"),sQuery(id+"F5.wireOp",EDGE,"E7.right"),sQuery(id+"F5.wireOp",EDGE,"E8"),sQuery(id+"F5.wireOp",EDGE,"E9"),sQuery(id+"F5.wireOp",EDGE,"E10"),sQuery(id+"F5.wireOp",EDGE,"E11")])],"isStart":true});
            var sketch = newSketch(context, id + "F17", { "sketchPlane" : qUnion([Q0])});
            skCircle(sketch, "E43", {"center": v(80.05, 4.56) * mm, "radius": 3 * mm});
            skLineSegment(sketch, "E44", {"start": v(80.05, 1.56) * mm, "end": v(84.05, 1.56) * mm});
            skLineSegment(sketch, "E45", {"start": v(77.05, 4.56) * mm, "end": v(77.05, 8.56) * mm});
            skCircle(sketch, "E46", {"center": v(80.05, -31.44) * mm, "radius": 3 * mm});
            skLineSegment(sketch, "E47", {"start": v(80.05, -28.44) * mm, "end": v(84.05, -28.44) * mm});
            skLineSegment(sketch, "E48", {"start": v(77.05, -31.44) * mm, "end": v(77.05, -35.44) * mm});
            skCircle(sketch, "E49", {"center": v(24.05, 4.56) * mm, "radius": 3 * mm});
            skCircle(sketch, "E50", {"center": v(24.05, -31.44) * mm, "radius": 3 * mm});
            skLineSegment(sketch, "E51", {"start": v(27.05, 4.56) * mm, "end": v(27.05, 8.56) * mm});
            skLineSegment(sketch, "E52", {"start": v(24.05, 1.56) * mm, "end": v(20.05, 1.56) * mm});
            skLineSegment(sketch, "E53", {"start": v(27.05, -31.44) * mm, "end": v(27.05, -35.44) * mm});
            skLineSegment(sketch, "E54", {"start": v(24.05, -28.44) * mm, "end": v(20.05, -28.44) * mm});
            skSolve(sketch);
        }
        {
            var Q0;
            Q0=qSketchRegion(id+"F17",true);
            var Q1;
            {var subQ4=sQuery(id+"F17.wireOp",EDGE,"E44");Q1=makeQuery(id+"F17.imprint","IMPRINT",FACE,{"disambiguationData":[TD([[makeQuery(id+"F17.imprint","IMPRINT",EDGE,{"derivedFrom":subQ4}),1.0]])]});}
            var Q2;
            {var subQ4=sQuery(id+"F17.wireOp",EDGE,"E47");Q2=makeQuery(id+"F17.imprint","IMPRINT",FACE,{"disambiguationData":[TD([[makeQuery(id+"F17.imprint","IMPRINT",EDGE,{"derivedFrom":subQ4}),-1.0]])]});}
            var Q3;
            {var subQ0=sQuery(id+"F17.wireOp",EDGE,"E51");Q3=makeQuery(id+"F17.imprint","IMPRINT",FACE,{"disambiguationData":[TD([[makeQuery(id+"F17.imprint","IMPRINT",EDGE,{"derivedFrom":subQ0}),1.0]])]});}
            var Q4;
            {var subQ3=sQuery(id+"F17.wireOp",EDGE,"E53");Q4=makeQuery(id+"F17.imprint","IMPRINT",FACE,{"disambiguationData":[TD([[makeQuery(id+"F17.imprint","IMPRINT",EDGE,{"derivedFrom":subQ3}),-1.0]])]});}
            extrude(context, id + "F18", {"entities" : qUnion([Q0, Q1, Q2, Q3, Q4]), "operationType" : NewBodyOperationType.REMOVE, "oppositeDirection" : true, "depth" : 8.5 * mm, "offsetDistance" : 25.4 * mm});
        }
        {
            var Q0;
            Q0=makeQuery(id+"F8.boolean.opBoolean","MERGE",FACE,{"derivedFrom":[makeQuery(id+"F6.opExtrude","SWEPT_FACE",FACE,{"disambiguationData":[OSD([sQuery(id+"F5.wireOp",EDGE,"E7.right")])]}),makeQuery(id+"F8.opExtrude","SWEPT_FACE",FACE,{"disambiguationData":[OSD([sQuery(id+"F7.wireOp",EDGE,"E16.right")])]})]});
            var sketch = newSketch(context, id + "F19", { "sketchPlane" : qUnion([Q0])});
            skCircle(sketch, "E55", {"center": v(13.44, 8) * mm, "radius": 2 * mm});
            skPoint(sketch, "E55.centerSnap0", {"position": v(13.44, 10) * mm});
            skLineSegment(sketch, "E56", {"start": v(11.44, 8) * mm, "end": v(11.44, 10) * mm});
            skLineSegment(sketch, "E57", {"start": v(15.44, 8) * mm, "end": v(15.44, 10) * mm});
            skLineSegment(sketch, "E58", {"start": v(15.44, 10) * mm, "end": v(11.44, 10) * mm});
            skSolve(sketch);
        }
        {
            var Q0;
            {var subQ0=sQuery(id+"F19.wireOp",EDGE,"E55");var subQ1=makeQuery(id+"F19.imprint","INTERSECT",VERTEX,{"derivedFrom":[subQ0,sQuery(id+"F19.wireOp",EDGE,"E57")]});Q0=makeQuery(id+"F19.imprint","IMPRINT",FACE,{"disambiguationData":[TD([[makeQuery(id+"F19.imprint","IMPRINT",EDGE,{"disambiguationData":[TD([[subQ1,-1.0]])],"derivedFrom":subQ0}),1.0]])]});}
            var Q1;
            {var subQ0=sQuery(id+"F19.wireOp",EDGE,"E57");Q1=makeQuery(id+"F19.imprint","IMPRINT",FACE,{"disambiguationData":[TD([[makeQuery(id+"F19.imprint","IMPRINT",EDGE,{"derivedFrom":subQ0}),1.0]])]});}
            var Q2;
            {var subQ0=sQuery(id+"F19.wireOp",EDGE,"E56");Q2=makeQuery(id+"F19.imprint","IMPRINT",FACE,{"disambiguationData":[TD([[makeQuery(id+"F19.imprint","IMPRINT",EDGE,{"derivedFrom":subQ0}),-1.0]])]});}
            extrude(context, id + "F20", {"entities" : qUnion([Q0, Q1, Q2]), "operationType" : NewBodyOperationType.REMOVE, "oppositeDirection" : true, "depth" : 25.4 * mm, "offsetDistance" : 25.4 * mm});
        }
        {
            var Q0;
            Q0=makeQuery(id+"F10.opExtrude","CAP_FACE",FACE,{"disambiguationData":[OSD([sQuery(id+"F9.wireOp",EDGE,"E18.bottom"),sQuery(id+"F9.wireOp",EDGE,"E18.top"),sQuery(id+"F9.wireOp",EDGE,"E18.left"),sQuery(id+"F9.wireOp",EDGE,"E18.right"),sQuery(id+"F9.wireOp",EDGE,"E19"),sQuery(id+"F9.wireOp",EDGE,"E20"),sQuery(id+"F9.wireOp",EDGE,"E21"),sQuery(id+"F9.wireOp",EDGE,"E22")])],"isStart":true});
            var sketch = newSketch(context, id + "F21", { "sketchPlane" : qUnion([Q0])});
            skCircle(sketch, "E59", {"center": v(45.8, 32.18) * mm, "radius": 1.5 * mm});
            skCircle(sketch, "E60", {"center": v(71.2, 32.18) * mm, "radius": 1.5 * mm});
            skPoint(sketch, "E61", {"position": v(53.5, 57.13) * mm});
            skPoint(sketch, "E62", {"position": v(58.5, 32.18) * mm});
            skCircle(sketch, "E63", {"center": v(45.8, 19.48) * mm, "radius": 1.5 * mm});
            skCircle(sketch, "E64", {"center": v(71.2, 19.48) * mm, "radius": 1.5 * mm});
            skSolve(sketch);
        }
        {
            var Q0;
            Q0 = qSketchRegion(id + "F21", true);
            extrude(context, id + "F22", {"entities" : qUnion([Q0]), "operationType" : NewBodyOperationType.REMOVE, "oppositeDirection" : true, "depth" : 25.4 * mm, "offsetDistance" : 25.4 * mm});
        }
        {
            var Q0;
            Q0=makeQuery(id+"F6.opExtrude","CAP_FACE",FACE,{"disambiguationData":[OSD([sQuery(id+"F5.wireOp",EDGE,"E7.bottom"),sQuery(id+"F5.wireOp",EDGE,"E7.top"),sQuery(id+"F5.wireOp",EDGE,"E7.left"),sQuery(id+"F5.wireOp",EDGE,"E7.right"),sQuery(id+"F5.wireOp",EDGE,"E8"),sQuery(id+"F5.wireOp",EDGE,"E9"),sQuery(id+"F5.wireOp",EDGE,"E10"),sQuery(id+"F5.wireOp",EDGE,"E11")])],"isStart":true});
            var sketch = newSketch(context, id + "F23", { "sketchPlane" : qUnion([Q0])});
            skLineSegment(sketch, "E65.bottom", {"start": v(20.05, -7.44) * mm, "end": v(29.05, -7.44) * mm});
            skLineSegment(sketch, "E65.top", {"start": v(20.05, -35.44) * mm, "end": v(29.05, -35.44) * mm});
            skLineSegment(sketch, "E65.left", {"start": v(20.05, -7.44) * mm, "end": v(20.05, -35.44) * mm});
            skLineSegment(sketch, "E65.right", {"start": v(29.05, -7.44) * mm, "end": v(29.05, -35.44) * mm});
            skSolve(sketch);
        }
        {
            var Q0;
            Q0 = qSketchRegion(id + "F23", true);
            extrude(context, id + "F24", {"entities" : qUnion([Q0]), "operationType" : NewBodyOperationType.ADD, "oppositeDirection" : true, "depth" : 4 * mm, "offsetDistance" : 25.4 * mm});
        }
        {
            var Q0;
            Q0=makeQuery(id+"F6.opExtrude","CAP_FACE",FACE,{"disambiguationData":[OSD([sQuery(id+"F5.wireOp",EDGE,"E7.bottom"),sQuery(id+"F5.wireOp",EDGE,"E7.top"),sQuery(id+"F5.wireOp",EDGE,"E7.left"),sQuery(id+"F5.wireOp",EDGE,"E7.right"),sQuery(id+"F5.wireOp",EDGE,"E8"),sQuery(id+"F5.wireOp",EDGE,"E9"),sQuery(id+"F5.wireOp",EDGE,"E10"),sQuery(id+"F5.wireOp",EDGE,"E11")])],"isStart":true});
            var sketch = newSketch(context, id + "F25", { "sketchPlane" : qUnion([Q0])});
            skLineSegment(sketch, "E66.bottom", {"start": v(20.05, -9.44) * mm, "end": v(27.05, -9.44) * mm});
            skLineSegment(sketch, "E66.top", {"start": v(20.05, -35.44) * mm, "end": v(27.05, -35.44) * mm});
            skLineSegment(sketch, "E66.left", {"start": v(20.05, -9.44) * mm, "end": v(20.05, -35.44) * mm});
            skLineSegment(sketch, "E66.right", {"start": v(27.05, -9.44) * mm, "end": v(27.05, -35.44) * mm});
            skSolve(sketch);
        }
        {
            var Q0;
            Q0 = qSketchRegion(id + "F25", true);
            extrude(context, id + "F26", {"entities" : qUnion([Q0]), "operationType" : NewBodyOperationType.REMOVE, "oppositeDirection" : true, "depth" : 2 * mm, "offsetDistance" : 25.4 * mm});
        }
        {
            var Q0;
            Q0=makeQuery(id+"F18.boolean.opBoolean","COPY",FACE,{"derivedFrom":makeQuery(id+"F18.opExtrude","CAP_FACE",FACE,{"disambiguationData":[OSD([sQuery(id+"F5.wireOp",EDGE,"E7.bottom"),sQuery(id+"F5.wireOp",EDGE,"E7.left"),sQuery(id+"F17.wireOp",EDGE,"E50"),sQuery(id+"F17.wireOp",EDGE,"E53"),sQuery(id+"F17.wireOp",EDGE,"E54")])],"isStart":false})});
            var sketch = newSketch(context, id + "F27", { "sketchPlane" : qUnion([Q0])});
            skLineSegment(sketch, "E67.bottom", {"start": v(20.05, -35.44) * mm, "end": v(27.05, -35.44) * mm});
            skLineSegment(sketch, "E67.top", {"start": v(20.05, -28.44) * mm, "end": v(27.05, -28.44) * mm});
            skLineSegment(sketch, "E67.left", {"start": v(20.05, -35.44) * mm, "end": v(20.05, -28.44) * mm});
            skLineSegment(sketch, "E67.right", {"start": v(27.05, -35.44) * mm, "end": v(27.05, -28.44) * mm});
            skCircle(sketch, "E68", {"center": v(24.05, -31.44) * mm, "radius": 3 * mm});
            skSolve(sketch);
        }
        {
            var Q0;
            {var subQ0=sQuery(id+"F5.wireOp",EDGE,"E8");Q0=makeQuery(id+"F27.imprint","IMPRINT",FACE,{"disambiguationData":[TD([[makeQuery(id+"F27.imprint","IMPRINT",EDGE,{"derivedFrom":makeQuery(id+"F18.boolean.opBoolean","INTERSECT",EDGE,{"derivedFrom":[makeQuery(id+"F8.boolean.opBoolean","MERGE",FACE,{"derivedFrom":[makeQuery(id+"F6.opExtrude","SWEPT_FACE",FACE,{"disambiguationData":[OSD([subQ0])]}),makeQuery(id+"F8.opExtrude","SWEPT_FACE",FACE,{"disambiguationData":[OSD([subQ0])]})]}),makeQuery(id+"F18.opExtrude","CAP_FACE",FACE,{"disambiguationData":[OSD([sQuery(id+"F5.wireOp",EDGE,"E7.bottom"),sQuery(id+"F5.wireOp",EDGE,"E7.left"),sQuery(id+"F17.wireOp",EDGE,"E50"),sQuery(id+"F17.wireOp",EDGE,"E53"),sQuery(id+"F17.wireOp",EDGE,"E54")])],"isStart":false})]})}),1.0]])]});}
            var Q1;
            {var subQ0=sQuery(id+"F27.wireOp",EDGE,"E68");var subQ1=makeQuery(id+"F27.imprint","INTERSECT",VERTEX,{"derivedFrom":[sQuery(id+"F27.wireOp",EDGE,"E67.right"),subQ0]});Q1=makeQuery(id+"F27.imprint","IMPRINT",FACE,{"disambiguationData":[TD([[makeQuery(id+"F27.imprint","IMPRINT",EDGE,{"disambiguationData":[TD([[subQ1,-1.0]])],"derivedFrom":subQ0}),1.0]])]});}
            var Q2;
            {var subQ3=sQuery(id+"F27.wireOp",EDGE,"E67.bottom");Q2=makeQuery(id+"F27.imprint","IMPRINT",FACE,{"disambiguationData":[TD([[makeQuery(id+"F27.imprint","IMPRINT",EDGE,{"derivedFrom":subQ3}),1.0]])]});}
            extrude(context, id + "F28", {"entities" : qUnion([Q0, Q1, Q2]), "operationType" : NewBodyOperationType.REMOVE, "depth" : 25.4 * mm, "offsetDistance" : 25.4 * mm});
        }
    });
